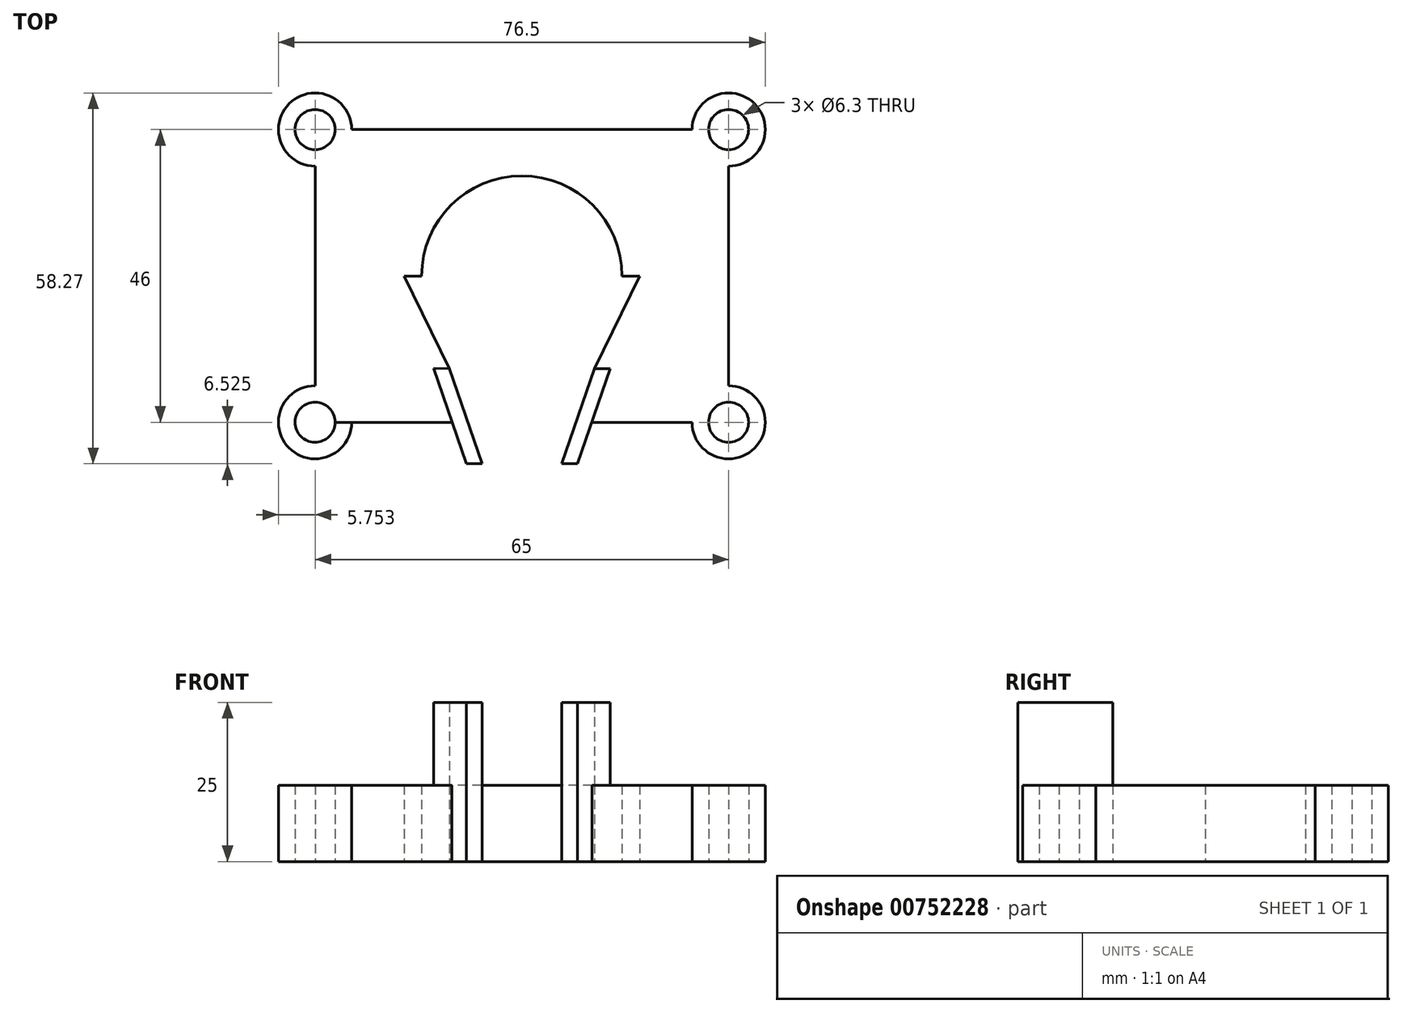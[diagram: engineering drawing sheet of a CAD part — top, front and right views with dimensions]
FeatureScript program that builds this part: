
annotation { "Feature Type Name" : "Feature", "Feature Type Description" : "" }
export const myFeature = defineFeature(function(context is Context, id is Id, definition is map)
    precondition{}
    {
        {
            var Q0;
            Q0=qCreatedBy(makeId("Top.planeOp"),FACE);
            var sketch = newSketch(context, id + "F0", { "sketchPlane" : qUnion([Q0])});
            skLineSegment(sketch, "E0.bottom", {"start": v(-52.67, 38.18) * mm, "end": v(6.03, 38.18) * mm});
            skLineSegment(sketch, "E0.top", {"start": v(-52.67, -7.82) * mm, "end": v(-34.3, -7.82) * mm});
            skLineSegment(sketch, "E0.left", {"start": v(-55.82, 35.03) * mm, "end": v(-55.82, -4.67) * mm});
            skLineSegment(sketch, "E0.right", {"start": v(9.18, 35.03) * mm, "end": v(9.18, -4.67) * mm});
            skCircle(sketch, "E1", {"center": v(9.18, 38.18) * mm, "radius": 3.15 * mm});
            skCircle(sketch, "E2", {"center": v(-55.82, 38.18) * mm, "radius": 3.15 * mm});
            skCircle(sketch, "E3", {"center": v(-55.82, -7.82) * mm, "radius": 3.15 * mm});
            skCircle(sketch, "E4", {"center": v(9.18, -7.82) * mm, "radius": 3.15 * mm});
            skCircle(sketch, "E5", {"center": v(-55.82, 38.18) * mm, "radius": 5.75 * mm});
            skCircle(sketch, "E6", {"center": v(9.18, 38.18) * mm, "radius": 5.75 * mm});
            skCircle(sketch, "E7", {"center": v(9.18, -7.82) * mm, "radius": 5.75 * mm});
            skCircle(sketch, "E8", {"center": v(-55.82, -7.82) * mm, "radius": 5.75 * mm});
            skPoint(sketch, "E9.first.point", {"position": v(-23.32, 38.18) * mm});
            skPoint(sketch, "E9.second.point", {"position": v(-55.82, 15.18) * mm});
            skLineSegment(sketch, "E10.top", {"start": v(-52.67, -7.85) * mm, "end": v(-34.3, -7.85) * mm});
            skPoint(sketch, "E10.middle", {"position": v(-23.32, 15.17) * mm});
            skCircle(sketch, "E11", {"center": v(-23.32, 15.17) * mm, "radius": 15.75 * mm});
            skArc(sketch, "E12", {"start": v(-4.82, 15.17) * mm, "mid": v(-23.32, 33.67) * mm, "end": v(-41.82, 15.17) * mm});
            skLineSegment(sketch, "E13", {"start": v(-23.32, -7.82) * mm, "end": v(-23.32, -7.85) * mm});
            skLineSegment(sketch, "E14", {"start": v(-34.71, 0.6) * mm, "end": v(-29.57, -14.34) * mm});
            skLineSegment(sketch, "E15", {"start": v(-17.07, -14.34) * mm, "end": v(-11.92, 0.6) * mm});
            skLineSegment(sketch, "E16", {"start": v(-29.57, -14.34) * mm, "end": v(-32.07, -14.34) * mm});
            skLineSegment(sketch, "E17", {"start": v(-32.07, -14.34) * mm, "end": v(-37.21, 0.64) * mm});
            skLineSegment(sketch, "E18", {"start": v(-37.21, 0.64) * mm, "end": v(-34.71, 0.6) * mm});
            skLineSegment(sketch, "E19", {"start": v(-17.07, -14.34) * mm, "end": v(-14.57, -14.34) * mm});
            skLineSegment(sketch, "E20", {"start": v(-14.57, -14.34) * mm, "end": v(-9.42, 0.6) * mm});
            skLineSegment(sketch, "E21", {"start": v(-9.42, 0.6) * mm, "end": v(-11.92, 0.6) * mm});
            skLineSegment(sketch, "E22.trimOffspring", {"start": v(-55.82, -7.82) * mm, "end": v(-55.82, -7.85) * mm});
            skPoint(sketch, "E23.orphan", {"position": v(9.18, -7.85) * mm});
            skLineSegment(sketch, "E24.trimOffspring", {"start": v(9.18, 38.18) * mm, "end": v(9.18, 38.18) * mm});
            skPoint(sketch, "E25.orphan", {"position": v(-23.32, -14.34) * mm});
            skLineSegment(sketch, "E26.trimOffspring", {"start": v(-12.32, -7.82) * mm, "end": v(6.03, -7.82) * mm});
            skLineSegment(sketch, "E27.trimOffspring", {"start": v(-12.33, -7.85) * mm, "end": v(6.03, -7.85) * mm});
            skLineSegment(sketch, "E28", {"start": v(-23.32, 15.17) * mm, "end": v(-41.82, 15.17) * mm});
            skLineSegment(sketch, "E29", {"start": v(-34.71, 0.6) * mm, "end": v(-41.82, 15.17) * mm});
            skLineSegment(sketch, "E30", {"start": v(-23.32, 15.17) * mm, "end": v(-4.82, 15.17) * mm});
            skLineSegment(sketch, "E31", {"start": v(-11.92, 0.6) * mm, "end": v(-4.82, 15.17) * mm});
            skLineSegment(sketch, "E32", {"start": v(-29.57, -14.34) * mm, "end": v(-17.07, -14.34) * mm});
            skLineSegment(sketch, "E33", {"start": v(-41.82, 15.17) * mm, "end": v(-55.82, 15.18) * mm});
            skLineSegment(sketch, "E34", {"start": v(-4.82, 15.17) * mm, "end": v(9.18, 15.17) * mm});
            skLineSegment(sketch, "E35", {"start": v(-23.32, 15.17) * mm, "end": v(-23.32, -14.34) * mm});
            skLineSegment(sketch, "E36", {"start": v(-23.32, 15.17) * mm, "end": v(-23.32, 38.18) * mm});
            skLineSegment(sketch, "E37", {"start": v(-34.71, 0.6) * mm, "end": v(-11.92, 0.6) * mm});
            skSolve(sketch);
        }
        {
            var Q0;
            {var subQ0=sQuery(id+"F0.wireOp",EDGE,"E33");Q0=makeQuery(id+"F0.imprint","IMPRINT",FACE,{"disambiguationData":[TD([[makeQuery(id+"F0.imprint","IMPRINT",EDGE,{"derivedFrom":subQ0}),-1.0]])]});}
            var Q1;
            {var subQ0=sQuery(id+"F0.wireOp",EDGE,"E0.bottom");var subQ1=sQuery(id+"F0.wireOp",EDGE,"E2");var subQ2=makeQuery(id+"F0.imprint","INTERSECT",VERTEX,{"derivedFrom":[subQ1,subQ0]});Q1=makeQuery(id+"F0.imprint","IMPRINT",FACE,{"disambiguationData":[TD([[makeQuery(id+"F0.imprint","IMPRINT",EDGE,{"disambiguationData":[TD([[subQ2,1.0]])],"derivedFrom":subQ1}),-1.0]])]});}
            var Q2;
            {var subQ0=sQuery(id+"F0.wireOp",EDGE,"E0.bottom");var subQ1=sQuery(id+"F0.wireOp",EDGE,"E2");var subQ2=makeQuery(id+"F0.imprint","INTERSECT",VERTEX,{"derivedFrom":[subQ1,subQ0]});Q2=makeQuery(id+"F0.imprint","IMPRINT",FACE,{"disambiguationData":[TD([[makeQuery(id+"F0.imprint","IMPRINT",EDGE,{"disambiguationData":[TD([[subQ2,-1.0]])],"derivedFrom":subQ1}),-1.0]])]});}
            var Q3;
            {var subQ0=sQuery(id+"F0.wireOp",EDGE,"E34");Q3=makeQuery(id+"F0.imprint","IMPRINT",FACE,{"disambiguationData":[TD([[makeQuery(id+"F0.imprint","IMPRINT",EDGE,{"derivedFrom":subQ0}),1.0]])]});}
            var Q4;
            {var subQ0=sQuery(id+"F0.wireOp",EDGE,"E36");var subQ1=sQuery(id+"F0.wireOp",EDGE,"E11");var subQ2=makeQuery(id+"F0.imprint","INTERSECT",VERTEX,{"derivedFrom":[subQ1,subQ0]});Q4=makeQuery(id+"F0.imprint","IMPRINT",FACE,{"disambiguationData":[TD([[makeQuery(id+"F0.imprint","IMPRINT",EDGE,{"disambiguationData":[TD([[subQ2,1.0]])],"derivedFrom":subQ1}),-1.0]])]});}
            var Q5;
            {var subQ0=sQuery(id+"F0.wireOp",EDGE,"E36");var subQ1=sQuery(id+"F0.wireOp",EDGE,"E11");var subQ2=makeQuery(id+"F0.imprint","INTERSECT",VERTEX,{"derivedFrom":[subQ1,subQ0]});Q5=makeQuery(id+"F0.imprint","IMPRINT",FACE,{"disambiguationData":[TD([[makeQuery(id+"F0.imprint","IMPRINT",EDGE,{"disambiguationData":[TD([[subQ2,-1.0]])],"derivedFrom":subQ1}),-1.0]])]});}
            var Q6;
            {var subQ0=sQuery(id+"F0.wireOp",EDGE,"E0.bottom");var subQ1=sQuery(id+"F0.wireOp",EDGE,"E1");var subQ2=makeQuery(id+"F0.imprint","INTERSECT",VERTEX,{"derivedFrom":[subQ1,subQ0]});Q6=makeQuery(id+"F0.imprint","IMPRINT",FACE,{"disambiguationData":[TD([[makeQuery(id+"F0.imprint","IMPRINT",EDGE,{"disambiguationData":[TD([[subQ2,1.0]])],"derivedFrom":subQ1}),-1.0]])]});}
            var Q7;
            {var subQ0=sQuery(id+"F0.wireOp",EDGE,"E0.bottom");var subQ1=sQuery(id+"F0.wireOp",EDGE,"E1");var subQ2=makeQuery(id+"F0.imprint","INTERSECT",VERTEX,{"derivedFrom":[subQ1,subQ0]});Q7=makeQuery(id+"F0.imprint","IMPRINT",FACE,{"disambiguationData":[TD([[makeQuery(id+"F0.imprint","IMPRINT",EDGE,{"disambiguationData":[TD([[subQ2,-1.0]])],"derivedFrom":subQ1}),-1.0]])]});}
            var Q8;
            {var subQ0=sQuery(id+"F0.wireOp",EDGE,"E0.right");var subQ1=sQuery(id+"F0.wireOp",EDGE,"E4");var subQ2=makeQuery(id+"F0.imprint","INTERSECT",VERTEX,{"derivedFrom":[subQ1,subQ0]});Q8=makeQuery(id+"F0.imprint","IMPRINT",FACE,{"disambiguationData":[TD([[makeQuery(id+"F0.imprint","IMPRINT",EDGE,{"disambiguationData":[TD([[subQ2,1.0]])],"derivedFrom":subQ1}),-1.0]])]});}
            var Q9;
            {var subQ0=sQuery(id+"F0.wireOp",EDGE,"E0.right");var subQ1=sQuery(id+"F0.wireOp",EDGE,"E4");var subQ2=makeQuery(id+"F0.imprint","INTERSECT",VERTEX,{"derivedFrom":[subQ1,subQ0]});Q9=makeQuery(id+"F0.imprint","IMPRINT",FACE,{"disambiguationData":[TD([[makeQuery(id+"F0.imprint","IMPRINT",EDGE,{"disambiguationData":[TD([[subQ2,-1.0]])],"derivedFrom":subQ1}),-1.0]])]});}
            var Q10;
            Q10=makeQuery(id+"F0.imprint","IMPRINT",FACE,{"disambiguationData":[TD([[makeQuery(id+"F0.imprint","IMPRINT",EDGE,{"derivedFrom":sQuery(id+"F0.wireOp",EDGE,"E15")}),-1.0]])]});
            var Q11;
            {var subQ0=sQuery(id+"F0.wireOp",EDGE,"E21");Q11=makeQuery(id+"F0.imprint","IMPRINT",FACE,{"disambiguationData":[TD([[makeQuery(id+"F0.imprint","IMPRINT",EDGE,{"derivedFrom":subQ0}),-1.0]])]});}
            var Q12;
            {var subQ8=sQuery(id+"F0.wireOp",EDGE,"E18");Q12=makeQuery(id+"F0.imprint","IMPRINT",FACE,{"disambiguationData":[TD([[makeQuery(id+"F0.imprint","IMPRINT",EDGE,{"derivedFrom":subQ8}),1.0]])]});}
            var Q13;
            {var subQ0=sQuery(id+"F0.wireOp",EDGE,"E3");var subQ1=sQuery(id+"F0.wireOp",EDGE,"E0.top");var subQ2=makeQuery(id+"F0.imprint","INTERSECT",VERTEX,{"derivedFrom":[subQ1,subQ0]});Q13=makeQuery(id+"F0.imprint","IMPRINT",FACE,{"disambiguationData":[TD([[makeQuery(id+"F0.imprint","IMPRINT",EDGE,{"disambiguationData":[TD([[subQ2,-1.0]])],"derivedFrom":subQ1}),1.0]])]});}
            var Q14;
            {var subQ0=sQuery(id+"F0.wireOp",EDGE,"E10.top");var subQ1=sQuery(id+"F0.wireOp",EDGE,"E3");var subQ2=makeQuery(id+"F0.imprint","INTERSECT",VERTEX,{"derivedFrom":[subQ1,subQ0]});Q14=makeQuery(id+"F0.imprint","IMPRINT",FACE,{"disambiguationData":[TD([[makeQuery(id+"F0.imprint","IMPRINT",EDGE,{"disambiguationData":[TD([[subQ2,1.0]])],"derivedFrom":subQ1}),-1.0]])]});}
            var Q15;
            Q15=makeQuery(id+"F0.imprint","IMPRINT",FACE,{"disambiguationData":[TD([[makeQuery(id+"F0.imprint","IMPRINT",EDGE,{"derivedFrom":sQuery(id+"F0.wireOp",EDGE,"E14")}),-1.0]])]});
            extrude(context, id + "F1", {"entities" : qUnion([Q0, Q1, Q2, Q3, Q4, Q5, Q6, Q7, Q8, Q9, Q10, Q11, Q12, Q13, Q14, Q15]), "depth" : 12 * mm, "offsetDistance" : 25 * mm});
        }
        {
            var Q0;
            Q0=makeQuery(id+"F0.imprint","IMPRINT",FACE,{"disambiguationData":[TD([[makeQuery(id+"F0.imprint","IMPRINT",EDGE,{"derivedFrom":sQuery(id+"F0.wireOp",EDGE,"E14")}),-1.0]])]});
            var Q1;
            Q1=makeQuery(id+"F0.imprint","IMPRINT",FACE,{"disambiguationData":[TD([[makeQuery(id+"F0.imprint","IMPRINT",EDGE,{"derivedFrom":sQuery(id+"F0.wireOp",EDGE,"E15")}),-1.0]])]});
            extrude(context, id + "F2", {"entities" : qUnion([Q0, Q1]), "operationType" : NewBodyOperationType.ADD, "depth" : 25 * mm, "offsetDistance" : 25 * mm});
        }
    });
